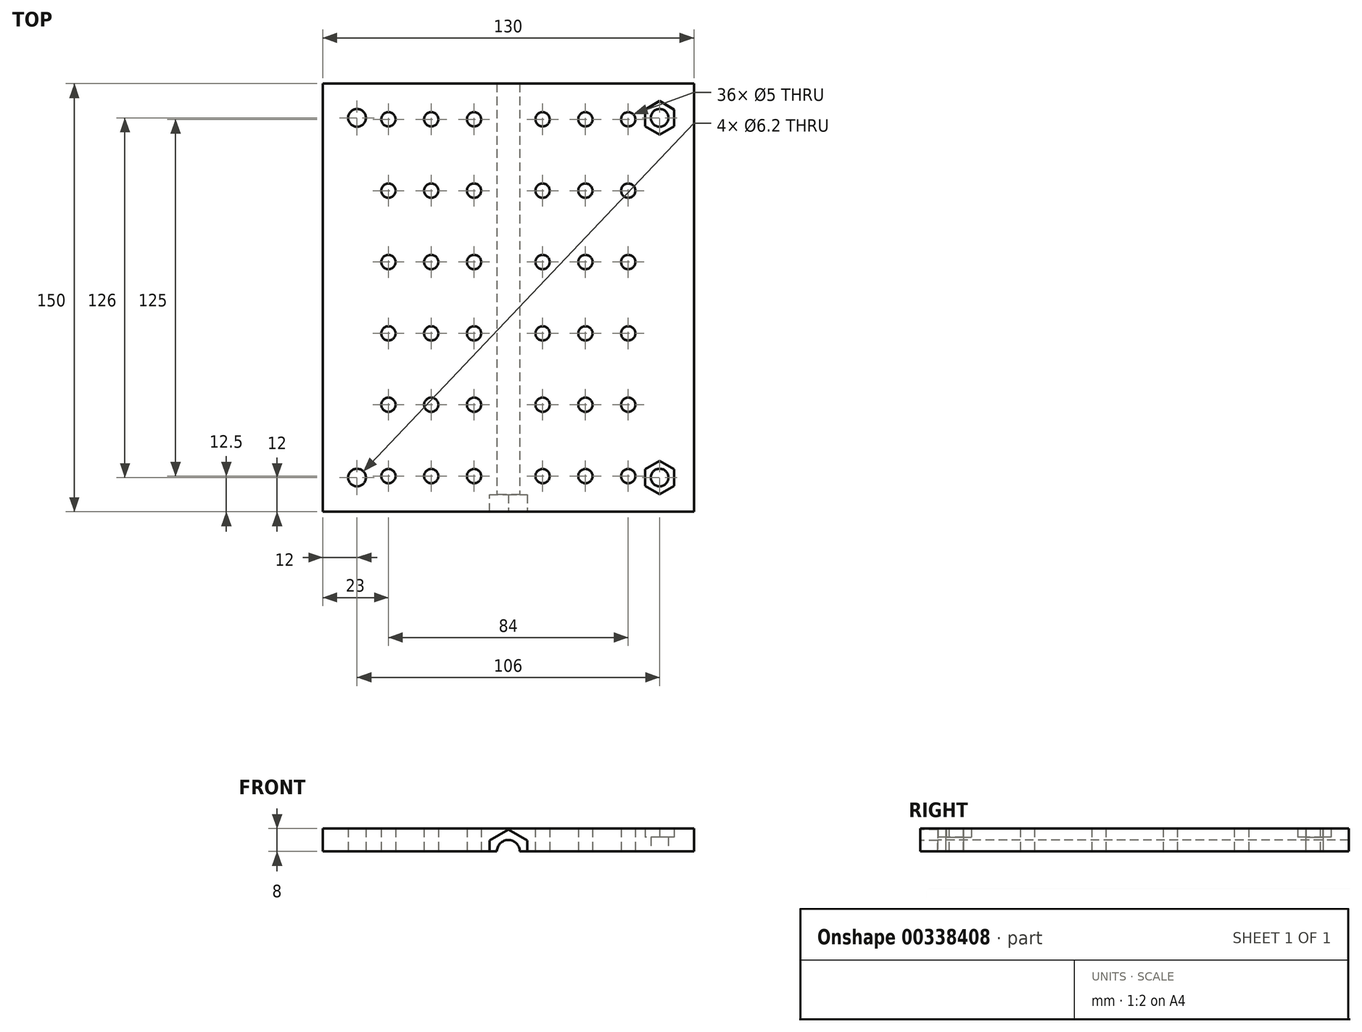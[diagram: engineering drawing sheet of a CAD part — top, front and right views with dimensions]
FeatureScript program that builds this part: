
annotation { "Feature Type Name" : "Feature", "Feature Type Description" : "" }
export const myFeature = defineFeature(function(context is Context, id is Id, definition is map)
    precondition{}
    {
        {
            var Q0;
            Q0=qCreatedBy(makeId("Top.planeOp"),FACE);
            var sketch = newSketch(context, id + "F0", { "sketchPlane" : qUnion([Q0])});
            skLineSegment(sketch, "E0", {"start": v(-65, 75) * mm, "end": v(65, 75) * mm});
            skLineSegment(sketch, "E1", {"start": v(65, 75) * mm, "end": v(65, -75) * mm});
            skLineSegment(sketch, "E2", {"start": v(65, -75) * mm, "end": v(-65, -75) * mm});
            skLineSegment(sketch, "E3", {"start": v(-65, -75) * mm, "end": v(-65, 75) * mm});
            skCircle(sketch, "E4", {"center": v(-53, 63) * mm, "radius": 3.1 * mm});
            skCircle(sketch, "E5.MirrorC", {"center": v(-53, -63) * mm, "radius": 3.1 * mm});
            skCircle(sketch, "E6.cCircle", {"center": v(53, 63) * mm, "radius": 5.1 * mm, "construction": true});
            skLineSegment(sketch, "E6.0", {"start": v(58.1, 60.06) * mm, "end": v(53, 57.11) * mm});
            skLineSegment(sketch, "E6.1", {"start": v(53, 57.11) * mm, "end": v(47.9, 60.06) * mm});
            skLineSegment(sketch, "E6.2", {"start": v(47.9, 60.06) * mm, "end": v(47.9, 65.94) * mm});
            skLineSegment(sketch, "E6.3", {"start": v(47.9, 65.94) * mm, "end": v(53, 68.89) * mm});
            skLineSegment(sketch, "E6.4", {"start": v(53, 68.89) * mm, "end": v(58.1, 65.94) * mm});
            skLineSegment(sketch, "E6.5", {"start": v(58.1, 65.94) * mm, "end": v(58.1, 60.06) * mm});
            skPoint(sketch, "E6.0.midPoint", {"position": v(55.55, 58.58) * mm});
            skCircle(sketch, "E7", {"center": v(53, 63) * mm, "radius": 3.1 * mm});
            skLineSegment(sketch, "E8.MirrorCS", {"start": v(58.1, -60.06) * mm, "end": v(53, -57.11) * mm});
            skLineSegment(sketch, "E9.MirrorCS", {"start": v(53, -57.11) * mm, "end": v(47.9, -60.06) * mm});
            skLineSegment(sketch, "E10.MirrorCS", {"start": v(47.9, -60.06) * mm, "end": v(47.9, -65.94) * mm});
            skLineSegment(sketch, "E11.MirrorCS", {"start": v(47.9, -65.94) * mm, "end": v(53, -68.89) * mm});
            skLineSegment(sketch, "E12.MirrorCS", {"start": v(53, -68.89) * mm, "end": v(58.1, -65.94) * mm});
            skLineSegment(sketch, "E13.MirrorCS", {"start": v(58.1, -65.94) * mm, "end": v(58.1, -60.06) * mm});
            skCircle(sketch, "E14.MirrorC", {"center": v(53, -63) * mm, "radius": 5.1 * mm, "construction": true});
            skCircle(sketch, "E15.MirrorC", {"center": v(53, -63) * mm, "radius": 3.1 * mm});
            skPoint(sketch, "E16.MirrorP", {"position": v(55.55, -58.58) * mm});
            skCircle(sketch, "E17", {"center": v(-42, 62.5) * mm, "radius": 2.5 * mm});
            skCircle(sketch, "E18.0.1.0", {"center": v(-42, 37.5) * mm, "radius": 2.5 * mm});
            skCircle(sketch, "E18.0.2.0", {"center": v(-42, 12.5) * mm, "radius": 2.5 * mm});
            skCircle(sketch, "E18.0.3.0", {"center": v(-42, -12.5) * mm, "radius": 2.5 * mm});
            skCircle(sketch, "E18.0.4.0", {"center": v(-42, -37.5) * mm, "radius": 2.5 * mm});
            skCircle(sketch, "E18.0.5.0", {"center": v(-42, -62.5) * mm, "radius": 2.5 * mm});
            skCircle(sketch, "E18.1.0.0", {"center": v(-27, 62.5) * mm, "radius": 2.5 * mm});
            skCircle(sketch, "E18.1.1.0", {"center": v(-27, 37.5) * mm, "radius": 2.5 * mm});
            skCircle(sketch, "E18.1.2.0", {"center": v(-27, 12.5) * mm, "radius": 2.5 * mm});
            skCircle(sketch, "E18.1.3.0", {"center": v(-27, -12.5) * mm, "radius": 2.5 * mm});
            skCircle(sketch, "E18.1.4.0", {"center": v(-27, -37.5) * mm, "radius": 2.5 * mm});
            skCircle(sketch, "E18.1.5.0", {"center": v(-27, -62.5) * mm, "radius": 2.5 * mm});
            skCircle(sketch, "E18.2.0.0", {"center": v(-12, 62.5) * mm, "radius": 2.5 * mm});
            skCircle(sketch, "E18.2.1.0", {"center": v(-12, 37.5) * mm, "radius": 2.5 * mm});
            skCircle(sketch, "E18.2.2.0", {"center": v(-12, 12.5) * mm, "radius": 2.5 * mm});
            skCircle(sketch, "E18.2.3.0", {"center": v(-12, -12.5) * mm, "radius": 2.5 * mm});
            skCircle(sketch, "E18.2.4.0", {"center": v(-12, -37.5) * mm, "radius": 2.5 * mm});
            skCircle(sketch, "E18.2.5.0", {"center": v(-12, -62.5) * mm, "radius": 2.5 * mm});
            skLineSegment(sketch, "E18.direction1", {"start": v(-42, 62.5) * mm, "end": v(-27, 62.5) * mm, "construction": true});
            skLineSegment(sketch, "E18.direction2", {"start": v(-42, 62.5) * mm, "end": v(-42, 37.5) * mm, "construction": true});
            skCircle(sketch, "E19.MirrorC", {"center": v(42, 62.5) * mm, "radius": 2.5 * mm});
            skCircle(sketch, "E20.MirrorC", {"center": v(27, 62.5) * mm, "radius": 2.5 * mm});
            skCircle(sketch, "E21.MirrorC", {"center": v(42, 37.5) * mm, "radius": 2.5 * mm});
            skCircle(sketch, "E22.MirrorC", {"center": v(12, 62.5) * mm, "radius": 2.5 * mm});
            skCircle(sketch, "E23.MirrorC", {"center": v(27, -12.5) * mm, "radius": 2.5 * mm});
            skCircle(sketch, "E24.MirrorC", {"center": v(12, -37.5) * mm, "radius": 2.5 * mm});
            skCircle(sketch, "E25.MirrorC", {"center": v(42, -12.5) * mm, "radius": 2.5 * mm});
            skCircle(sketch, "E26.MirrorC", {"center": v(27, -62.5) * mm, "radius": 2.5 * mm});
            skCircle(sketch, "E27.MirrorC", {"center": v(12, -12.5) * mm, "radius": 2.5 * mm});
            skCircle(sketch, "E28.MirrorC", {"center": v(27, 12.5) * mm, "radius": 2.5 * mm});
            skCircle(sketch, "E29.MirrorC", {"center": v(42, 12.5) * mm, "radius": 2.5 * mm});
            skCircle(sketch, "E30.MirrorC", {"center": v(27, -37.5) * mm, "radius": 2.5 * mm});
            skCircle(sketch, "E31.MirrorC", {"center": v(27, 37.5) * mm, "radius": 2.5 * mm});
            skCircle(sketch, "E32.MirrorC", {"center": v(12, 12.5) * mm, "radius": 2.5 * mm});
            skCircle(sketch, "E33.MirrorC", {"center": v(12, -62.5) * mm, "radius": 2.5 * mm});
            skCircle(sketch, "E34.MirrorC", {"center": v(42, -62.5) * mm, "radius": 2.5 * mm});
            skCircle(sketch, "E35.MirrorC", {"center": v(42, -37.5) * mm, "radius": 2.5 * mm});
            skCircle(sketch, "E36.MirrorC", {"center": v(12, 37.5) * mm, "radius": 2.5 * mm});
            skLineSegment(sketch, "E37.MirrorCS", {"start": v(42, 62.5) * mm, "end": v(42, 37.5) * mm, "construction": true});
            skLineSegment(sketch, "E38.MirrorCS", {"start": v(42, 62.5) * mm, "end": v(27, 62.5) * mm, "construction": true});
            skLineSegment(sketch, "E39", {"start": v(-70.59, 0) * mm, "end": v(77.99, 0) * mm, "construction": true});
            skPoint(sketch, "E39.endSnap0", {"position": v(-65, 0) * mm});
            skSolve(sketch);
        }
        {
            var Q0;
            Q0=makeQuery(id+"F0.imprint","IMPRINT",FACE,{"disambiguationData":[TD([[makeQuery(id+"F0.imprint","IMPRINT",EDGE,{"derivedFrom":sQuery(id+"F0.wireOp",EDGE,"E0")}),-1.0]])]});
            var Q1;
            Q1=makeQuery(id+"F0.imprint","IMPRINT",FACE,{"disambiguationData":[TD([[makeQuery(id+"F0.imprint","IMPRINT",EDGE,{"derivedFrom":sQuery(id+"F0.wireOp",EDGE,"E6.0")}),-1.0]])]});
            var Q2;
            Q2=makeQuery(id+"F0.imprint","IMPRINT",FACE,{"disambiguationData":[TD([[makeQuery(id+"F0.imprint","IMPRINT",EDGE,{"derivedFrom":sQuery(id+"F0.wireOp",EDGE,"E8.MirrorCS")}),1.0]])]});
            extrude(context, id + "F1", {"entities" : qUnion([Q0, Q1, Q2]), "depth" : 8 * mm});
        }
        {
            var Q0;
            Q0=makeQuery(id+"F0.imprint","IMPRINT",FACE,{"disambiguationData":[TD([[makeQuery(id+"F0.imprint","IMPRINT",EDGE,{"derivedFrom":sQuery(id+"F0.wireOp",EDGE,"E6.0")}),-1.0]])]});
            var Q1;
            Q1=makeQuery(id+"F0.imprint","IMPRINT",FACE,{"disambiguationData":[TD([[makeQuery(id+"F0.imprint","IMPRINT",EDGE,{"derivedFrom":sQuery(id+"F0.wireOp",EDGE,"E8.MirrorCS")}),1.0]])]});
            extrude(context, id + "F2", {"entities" : qUnion([Q0, Q1]), "operationType" : NewBodyOperationType.REMOVE, "depth" : 25 * mm, "hasSecondDirection" : true, "secondDirectionOppositeDirection" : false, "secondDirectionDepth" : 5 * mm});
        }
        {
            var Q0;
            Q0=makeQuery(id+"F1.opExtrude","SWEPT_FACE",FACE,{"disambiguationData":[OSD([sQuery(id+"F0.wireOp",EDGE,"E2")])]});
            var sketch = newSketch(context, id + "F3", { "sketchPlane" : qUnion([Q0])});
            skCircle(sketch, "E40", {"center": v(0, 0) * mm, "radius": 4 * mm});
            skCircle(sketch, "E41.cCircle", {"center": v(0, 0) * mm, "radius": 6.6 * mm, "construction": true});
            skLineSegment(sketch, "E41.0", {"start": v(6.6, 3.81) * mm, "end": v(6.6, -3.81) * mm});
            skLineSegment(sketch, "E41.1", {"start": v(6.6, -3.81) * mm, "end": v(0, -7.62) * mm});
            skLineSegment(sketch, "E41.2", {"start": v(0, -7.62) * mm, "end": v(-6.6, -3.81) * mm});
            skLineSegment(sketch, "E41.3", {"start": v(-6.6, -3.81) * mm, "end": v(-6.6, 3.81) * mm});
            skLineSegment(sketch, "E41.4", {"start": v(-6.6, 3.81) * mm, "end": v(0, 7.62) * mm});
            skLineSegment(sketch, "E41.5", {"start": v(0, 7.62) * mm, "end": v(6.6, 3.81) * mm});
            skPoint(sketch, "E41.0.midPoint", {"position": v(6.6, 0) * mm});
            skSolve(sketch);
        }
        {
            var Q0;
            {var subQ0=sQuery(id+"F3.wireOp",EDGE,"E40");var subQ1=makeQuery(id+"F1.opExtrude","CAP_EDGE",EDGE,{"disambiguationData":[OSD([sQuery(id+"F0.wireOp",EDGE,"E2")])],"isStart":true});var subQ2=makeQuery(id+"F3.imprint","INTERSECT",VERTEX,{"disambiguationData":[OD(0.0)],"derivedFrom":[subQ1,subQ0]});Q0=makeQuery(id+"F3.imprint","IMPRINT",FACE,{"disambiguationData":[TD([[makeQuery(id+"F3.imprint","IMPRINT",EDGE,{"disambiguationData":[TD([[subQ2,-1.0]])],"derivedFrom":subQ0}),1.0]])]});}
            extrude(context, id + "F4", {"entities" : qUnion([Q0]), "operationType" : NewBodyOperationType.REMOVE, "endBound" : BoundingType.THROUGH_ALL, "oppositeDirection" : true, "depth" : 25 * mm});
        }
        {
            var Q0;
            {var subQ1=sQuery(id+"F3.wireOp",EDGE,"E41.3");Q0=makeQuery(id+"F3.imprint","IMPRINT",FACE,{"disambiguationData":[TD([[makeQuery(id+"F3.imprint","IMPRINT",EDGE,{"derivedFrom":subQ1}),-1.0]])]});}
            extrude(context, id + "F5", {"entities" : qUnion([Q0]), "operationType" : NewBodyOperationType.REMOVE, "oppositeDirection" : true, "depth" : 6 * mm});
        }
    });
